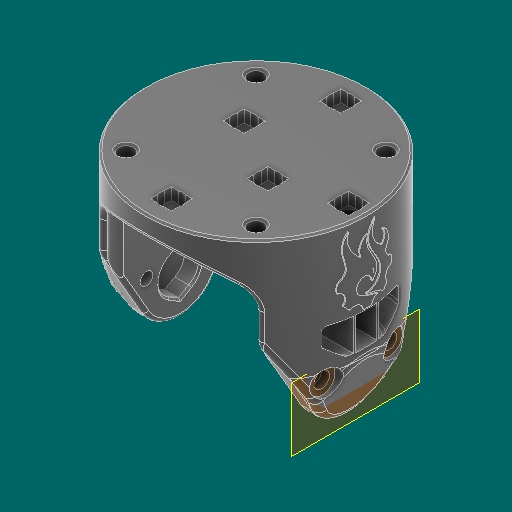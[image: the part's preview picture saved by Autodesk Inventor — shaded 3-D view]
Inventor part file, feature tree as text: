
AUTODESK INVENTOR PART (.ipt)
format: ipt  version: 2023.1 (Build 271208000, 208)  size: 1,954,304 bytes
history: native  units: in
note: dims shown in document units (in); Inventor stores cm internally (conversion verified against a paired STEP export)
features: sketch x14, other x13, plane x5
ambient origin geometry x8: Origin, YZ Plane, XZ Plane, XY Plane, X Axis, Y Axis, Z Axis, Center Point
bodies: Solid5 (feature_tree), Solid6 (feature_tree), Solid1 (feature_tree), Solid3 (feature_tree)
feature tree (32):
  other  "Carriage.ipt"
  other  "Solid1::Carriage.ipt"
  other  "Solid2::Carriage.ipt"
  other  "Solid3::Carriage.ipt"
  other  "Solid4::Carriage.ipt"
  other  "Solid5::Carriage.ipt"
  other  "TaggingFeature1"
  sketch  "Sketch2"  dims[d0=0.3937in]
  sketch  "Sketch3"
  sketch  "Sketch5"
  sketch  "Sketch11"
  sketch  "Sketch6"
  sketch  "Sketch7"
  sketch  "Sketch8"
  sketch  "Sketch9"
  sketch  "Sketch13"
  sketch  "Sketch14"
  sketch  "Sketch16"
  sketch  "Sketch17"
  sketch  "Sketch18"
  sketch  "Sketch19"
  plane  "Work Plane1"
  plane  "Work Plane3"
  plane  "Work Plane4"
  plane  "Work Plane5"
  plane  "Work Plane6"
  other  "Work Axis1"
  other  "Work Axis2"
  other  "Srf1"
  other  "Srf2"
  other  "Srf1::Derived"
  other  "Srf2::Derived"
